# Revit family: Legrand_Gestion_eclairage_Detecteur_Presence_Mur_autonome
name_source: partatom
category: Dispositifs d'éclairage
units: mm (PartAtom-declared; Revit-internal decimal feet)

## family parameters
Conserver l'orientation des annotations = Oui
Cote de connecteur circulaire = Utiliser le diamètre
Couper avec des vides une fois chargée = Non
Hôte = Face
Partagée = Non
Point de calcul de pièce = Non
Type d'élément = Normal

## types (4) — shared parameters
Collecteur de terre = Non
Condition Générale d'Utilisation = https://export.legrand.com
Cosses d'artère secondaire = Non
Couleur = Blanc
Durée d'enclenchement min. (s) = 5
Elévation par défaut = 2500 mm  [stored 8.2021 ft]
Fabricant = Legrand
Fréquence (MAX) (Hz) = 60
Fréquence (MIN) (Hz) = 50
Gestion CVC = Non
Hauteur de montage maximale (m) = 2.5
Liaison neutre = Non
Réglage de lumière constante = Oui
Sensibilité lumineuse (MAX) (lx) = 1275
Sensibilité lumineuse (MIN) (lx) = 5
Sensibilité lumineuse réglable = Oui
Sensibilité réglable = Oui
Température (MAX) (°C) = 45
Température (MIN) (°C) = -5
Tension nominale (V) = 230
Télécommandable = Oui
URL = http://www.legrandoc.com

## per-type parameters (varying)
| type | Adapté pour transmission sans fil | Angle de détection horizontal (MAX) (°) | Angle de détection horizontal (MIN) (°) | Capacité de coupure max. (W) | Classe de protection (IP) | Couloir | Coupure forcée | Courant de démarrage max. (A) | Description | Diamètre de détection sur le plancher (m) | Durée d'enclenchement max. (mn) | Entrée secondaire | Exécution - Modèle | Fonction variateur intégré | Gestion alarme | IP 42 - Modelisation 9 | IP42 ECO 2 PIR/US | IP55 ECO 2 | Mode de montage | Modèle | Numéro RAL | Portée max. frontale (m) | Portée max. latérale (m) | Type de tension |
| IP42 ECO 2 PIR/US | Oui | 180 | 180 | 0 | IP42 | Non | Oui | 0 | Détect autonome ECO2 Prog Mosaic-IR/US-1 circ éclair-saillie mur-IP42-8m frontal | 12 | 60 | Non | détecteur de présence | Oui | Non | Non | Oui | Non | encastré | 048916 | 9006 | 8 | 8 |  |
| IP55 ECO 2 | Non | 360 | 0 | 2000 | IP55 | Non | Non | 8.5 | Ecodétecteur autonome ECO 2 1 circuit - IR - saillie mur/plafond -IP 55 - 20 m | 8 | 59 | Oui | détecteur de mouvement | Non | Oui | Non | Non | Oui | apparent | 048933 | 9003 | 15 | 5 | CA |
| IP42 | Oui | 180 | 180 | 0 | IP42 | Non | Oui | 0 | DET ECO2 180 IR IP42 HTE SENS | 12 | 60 | Non | détecteur de présence | Oui | Non | Oui | Non | Non | encastré | 048914 | 9006 | 20 | 12 |  |
| Couloir IP42 ECO | Oui | 180 | 180 | 0 | IP42 | Oui | Oui | 0 | Détect autonome ECO 2 Prog Mosaic- IR- 1 circuit éclairage-saillie mur- IP42-20m | 12 | 60 | Non | détecteur de présence | Oui | Non | Oui | Non | Non | encastré | 048917 | 9006 | 20 | 12 |  |

note: [stored X ft] marks values corroborated as IEEE doubles in the binary element streams (Revit-internal decimal feet)
